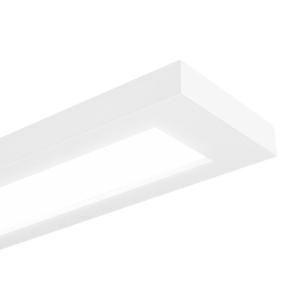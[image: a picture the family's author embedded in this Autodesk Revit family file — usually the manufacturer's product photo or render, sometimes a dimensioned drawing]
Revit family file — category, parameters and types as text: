
# Revit family: 3f_filippi_-_3f_travetta_op_3f_filippi_-_10732_-_3f_travetta_led_1x22w_op_l1590
name_source: partatom
category: Lighting Fixtures
units: mm (PartAtom-declared; Revit-internal decimal feet)

## family parameters
Cut with Voids When Loaded = No
Host = Face
Light Source = No
Part Type = Normal
Room Calculation Point = No
Round Connector Dimension = Use Diameter
Shared = No

## types (1)
- 3F Filippi - 3F Travetta OP (1 x LED, 2920 lm, 24.5 W, 4000 K)
    Apparent Load = 25 VA
    Approval mark = ENEC
    CIE Flux Codes = 49 81 97 100 100
    Color Rendering = 80
    Color Temperature = 4000 K
    Control Gear = Electronic ballast
    Default Elevation = 1800 mm
    Description = ILLUMINOTECHNICAL
Luminous efficiency 100% (DLOR 100%, ULOR 0%).
Initial luminous flux of the luminaire 2920 lm.
Direct symmetric distribution.
Installation Interdistance Transv.D = 1.20 x hu - Long.D = 1.20 x hu.
Tabular UGR (CIE 117 - 4H-8H; S=0.25H; 70/50/20): RUG 21 - 21.8.
Beam angle: 105° - 107°.
Luminous efficacy 119 lm/W.
Lifetime (L93/B10): 30000 h. (tq+25°C)
Lifetime (L90/B10): 50000 h. (tq+25°C)
Lifetime (L85/B10): 80000 h. (tq+25°C)
Lifetime (L80/B10): 100000 h. (tq+25°C)
Sudden decreased luminous flux after 50000 hours: 0% (C0).
Photobiological safety in compliance with IEC/TR 62778: RG0 risk exempt, (IEC 62471).
In compliance with IEC/EN 62722-2-1 - IEC/EN 62717 standards.

SOURCE
Linear LED module 22W/840.
Energy efficiency class (UE 2019/2020 - UE 2019/2015): D.
CIE 13.3 Colour rendering index: CRI >80 (R9 <50%).
IES TM-30 Fidelity Index: Rf = 84 Rg = 95.
CCT nominal colour temperature 4000 K.
Colour initial tolerance (MacAdam): SDCM 2.

MECHANICAL
Housing with squared shape in white painted galvannealed steel, with nonreflecting surface.
Flow recuperator in semi-glossy aluminium.
Opal methacrylate (PMMA) flat diffuser, anti-glare.
Luminaire with limited surface temperature. - D - (EN 60598-2-24)
Dimensions: 1590x190 mm, height 60 mm (edge 40 mm). Weight 5.105 kg.
IP20 protection degree.
Glow-wire test resistance 650°C.

ELECTRICAL
Halogen Free electronic wiring 230V-50/60Hz, power factor 0.90, THD <25%, constant output current, SELV, class I, 1 driver.
Power of the luminaire 24.5 W.
CE - IEC 60598-1 - EN 60598-1.
SAFE FLICKER: PstLM=<1 and SVM=<0.4 (IEC TR 61547-1 and IEC TR 63158), to ensure a more comfortable and safe light.
Luminaire compliant with EN 60598-2-22 for power supply from a centralised emergency system CPSS (Central Power Supply System), not incorporated in the luminaire - high risk areas excluded. The default power and flux are 100% in AC and 100% in DC.
Ambient temperature from 0°C to +25°C.
Temperature class T6 max 85°C.
5-pole terminal block for cascade line connection with connection capacity 2x2.5 mm².
Relative humidity UR: <85%.

INSTALLATION
Ceiling / Suspended.
All accessories dedicated to this product are available on the Catalog and on our website www.3F-Filippi.com.

APPLICATIONS
In environments, even with reduced height, requiring a comfortable light.
Exhibitions area, halls, great halls and shops.

WARNING
Luminaire designed for disposal/recycling at end-of-life.
Replaceable (LED only) light source by a professional. Replaceable control gear by a professional.
    Height = 60 mm  [stored 0.19685 ft]
    Lamp = 1 x LED
    Lamp Light Flux = 2920 lm
    Lamp Power = 24.5 W
    Lamp count = 1
    Length = 1590 mm
    Lifetime = 50000 h
    Luminous efficacy = 119 lm/W
    Manufacturer = 3F Filippi
    ModVariant = No
    Model = 3F Filippi - 10732 - 3F Travetta LED 1x22W OP L1590
    Mounting Place = Ceiling
    Mounting Type = Pendant
    Number of Poles = 1
    OnlyDefault = Yes
    Power Factor = 1
    Product Name = 3F Filippi - 3F Travetta OP
    Product group = pendant luminaire
    ProductGroupID = 9
    Protection Class = Protection class I
    Protection Degree = IP 20
    RLX_Detail_Level = 1
    RLX_Emergency_Light_Flux = 0 lm
    RLX_Emergency_Type = 0
    RLX_Emergency_Type_DB = No
    RlxData = <blob elided: 32481 chars, md5=b6382fd9>
    Socket = socket
    Standby Power = 0 W
    System Light Flux = 2920 lm
    System Power = 25 W
    Type Comments = Product without accessories
    Type Image = 3ffilippi_3f_travetta_led_op.jpg
    URL = http://relux.com
    VarID = ---
    Voltage = 0 V
    Weight = 0.00 kg
    Width = 190 mm  [stored 0.62336 ft]

note: [stored X ft] marks values corroborated as IEEE doubles in the binary element streams (Revit-internal decimal feet)

## geometry (parser evidence)
native form markers: Blend x4, Sweep x12
no freeform markers — native parametric forms only
